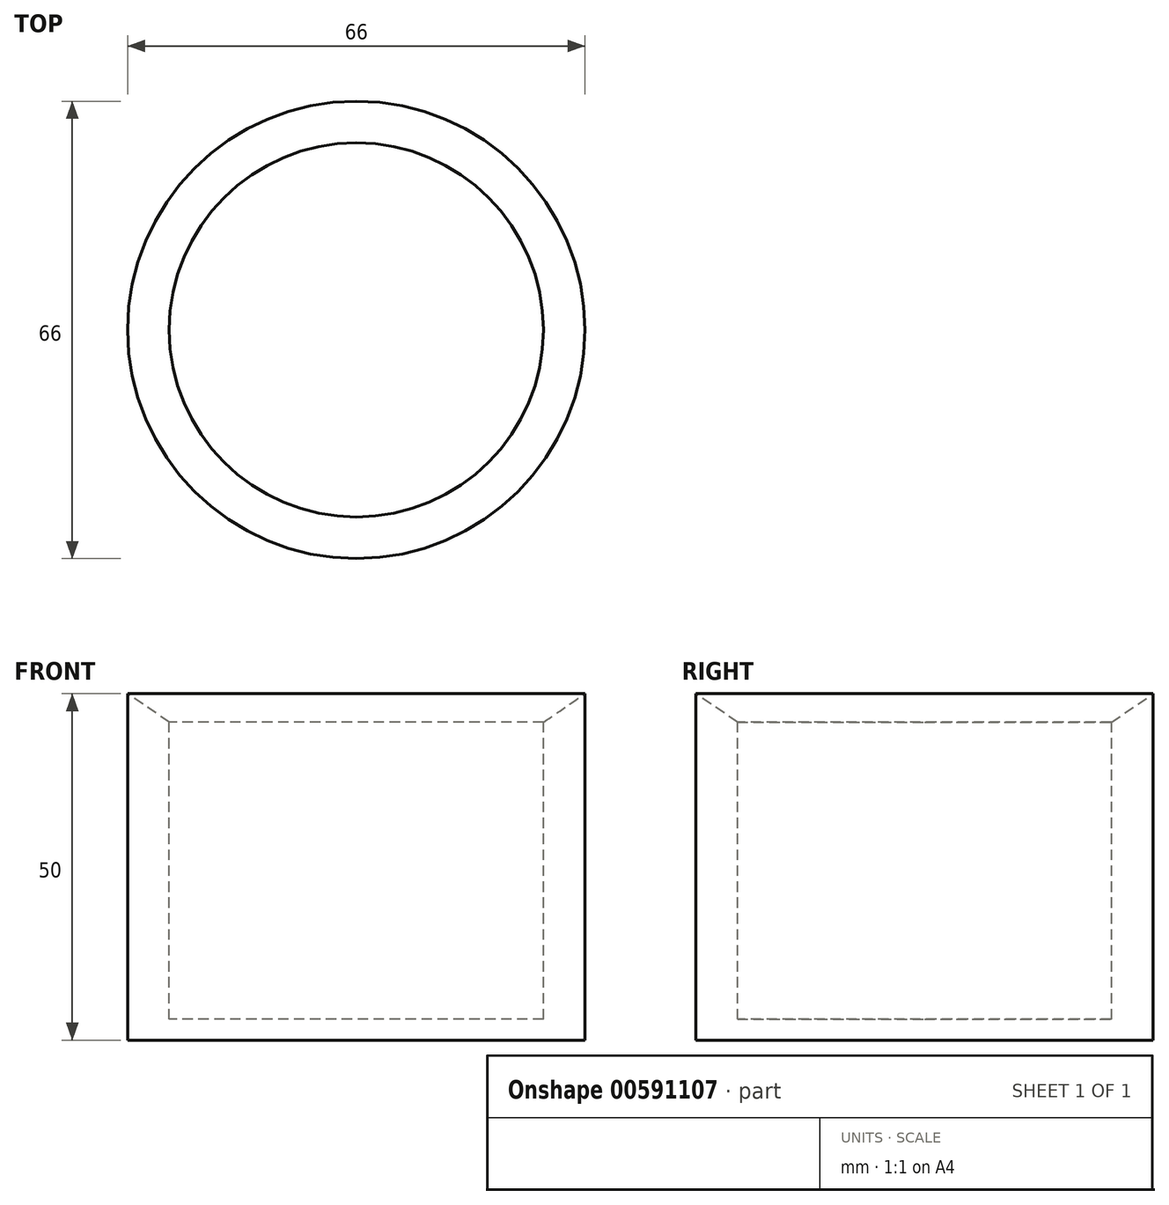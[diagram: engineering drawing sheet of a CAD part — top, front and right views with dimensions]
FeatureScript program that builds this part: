
annotation { "Feature Type Name" : "Feature", "Feature Type Description" : "" }
export const myFeature = defineFeature(function(context is Context, id is Id, definition is map)
    precondition{}
    {
        {
            var Q0;
            Q0=qCreatedBy(makeId("Right.planeOp"),FACE);
            var sketch = newSketch(context, id + "F0", { "sketchPlane" : qUnion([Q0])});
            skLineSegment(sketch, "E0", {"start": v(0, 0) * mm, "end": v(0, -3) * mm});
            skLineSegment(sketch, "E1", {"start": v(0, -3) * mm, "end": v(-33, -3) * mm});
            skLineSegment(sketch, "E2", {"start": v(-33, -3) * mm, "end": v(-33, 47) * mm});
            skLineSegment(sketch, "E3", {"start": v(-33, 47) * mm, "end": v(-27, 42.89) * mm});
            skLineSegment(sketch, "E4", {"start": v(-27, 42.89) * mm, "end": v(-27, 0) * mm});
            skLineSegment(sketch, "E5", {"start": v(0, 0) * mm, "end": v(-27, 0) * mm});
            skSolve(sketch);
        }
        {
            var Q0;
            Q0=makeQuery(id+"F0.imprint","IMPRINT",FACE,{"disambiguationData":[TD([[makeQuery(id+"F0.imprint","IMPRINT",EDGE,{"derivedFrom":sQuery(id+"F0.wireOp",EDGE,"E0")}),-1.0]])]});
            var Q1;
            Q1=sQuery(id+"F0.wireOp",EDGE,"E0");
            revolve(context, id + "F1", {"entities" : qUnion([Q0]), "axis" : qUnion([Q1]), "revolveType" : RevolveType.FULL});
        }
    });
